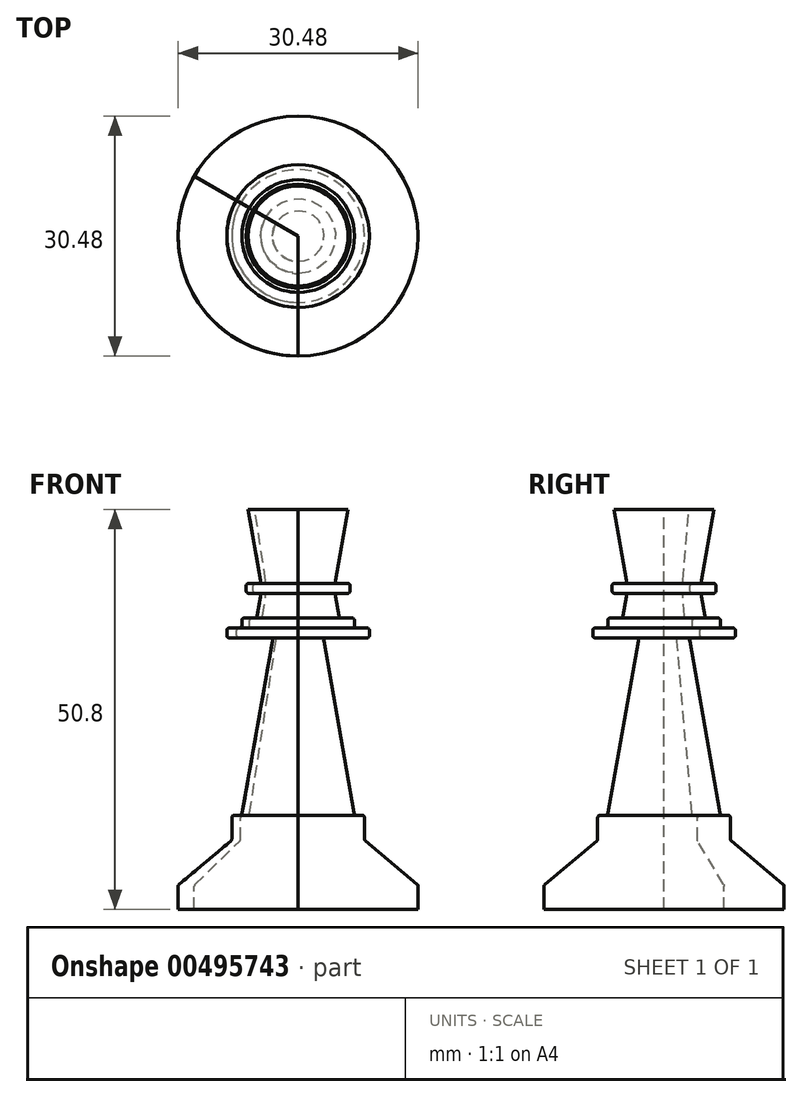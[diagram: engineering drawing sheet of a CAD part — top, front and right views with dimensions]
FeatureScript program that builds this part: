
annotation { "Feature Type Name" : "Feature", "Feature Type Description" : "" }
export const myFeature = defineFeature(function(context is Context, id is Id, definition is map)
    precondition{}
    {
        {
            var Q0;
            Q0=qCreatedBy(makeId("Front.planeOp"),FACE);
            var sketch = newSketch(context, id + "F0", { "sketchPlane" : qUnion([Q0])});
            skLineSegment(sketch, "E0.bottom", {"start": v(0, 0) * mm, "end": v(-15.24, 0) * mm});
            skLineSegment(sketch, "E0.top", {"start": v(0, 50.8) * mm, "end": v(-6.35, 50.8) * mm});
            skLineSegment(sketch, "E0.left", {"start": v(0, 0) * mm, "end": v(0, 50.8) * mm});
            skLineSegment(sketch, "E1", {"start": v(-15.24, 0) * mm, "end": v(-15.24, 2.93) * mm});
            skLineSegment(sketch, "E2", {"start": v(-15.13, 3.18) * mm, "end": v(-8.54, 8.7) * mm});
            skLineSegment(sketch, "E3", {"start": v(-8.43, 8.94) * mm, "end": v(-8.43, 11.65) * mm});
            skLineSegment(sketch, "E4", {"start": v(-8.11, 11.97) * mm, "end": v(-7.43, 11.97) * mm});
            skLineSegment(sketch, "E5", {"start": v(-7.11, 12.23) * mm, "end": v(-3.26, 34.11) * mm});
            skLineSegment(sketch, "E6", {"start": v(-3.57, 34.48) * mm, "end": v(-8.74, 34.48) * mm});
            skLineSegment(sketch, "E7", {"start": v(-9.06, 34.8) * mm, "end": v(-9.06, 35.44) * mm});
            skLineSegment(sketch, "E8", {"start": v(-8.74, 35.75) * mm, "end": v(-7.47, 35.75) * mm});
            skLineSegment(sketch, "E9", {"start": v(-7.15, 36.07) * mm, "end": v(-7.15, 36.7) * mm});
            skLineSegment(sketch, "E10", {"start": v(-6.83, 37.02) * mm, "end": v(-5.51, 37.02) * mm});
            skLineSegment(sketch, "E11", {"start": v(-5.2, 37.29) * mm, "end": v(-4.76, 39.78) * mm});
            skLineSegment(sketch, "E12", {"start": v(-5.07, 40.15) * mm, "end": v(-6.28, 40.15) * mm});
            skLineSegment(sketch, "E13", {"start": v(-6.6, 40.47) * mm, "end": v(-6.6, 41.1) * mm});
            skLineSegment(sketch, "E14", {"start": v(-6.28, 41.42) * mm, "end": v(-5.07, 41.42) * mm});
            skLineSegment(sketch, "E15", {"start": v(-4.76, 41.8) * mm, "end": v(-6.35, 50.8) * mm});
            skPoint(sketch, "E16.visualSharp", {"position": v(-15.24, 3.08) * mm});
            skArc(sketch, "E16.filletArc", {"start": v(-15.13, 3.18) * mm, "mid": v(-15.21, 3.07) * mm, "end": v(-15.24, 2.93) * mm});
            skPoint(sketch, "E17.visualSharp", {"position": v(-8.43, 8.8) * mm});
            skArc(sketch, "E17.filletArc", {"start": v(-8.54, 8.7) * mm, "mid": v(-8.46, 8.8) * mm, "end": v(-8.43, 8.94) * mm});
            skPoint(sketch, "E18.visualSharp", {"position": v(-3.2, 34.48) * mm});
            skArc(sketch, "E18.filletArc", {"start": v(-3.26, 34.11) * mm, "mid": v(-3.33, 34.37) * mm, "end": v(-3.57, 34.48) * mm});
            skPoint(sketch, "E19.visualSharp", {"position": v(-8.43, 11.97) * mm});
            skArc(sketch, "E19.filletArc", {"start": v(-8.11, 11.97) * mm, "mid": v(-8.34, 11.88) * mm, "end": v(-8.43, 11.65) * mm});
            skPoint(sketch, "E20.visualSharp", {"position": v(-7.16, 11.97) * mm});
            skArc(sketch, "E20.filletArc", {"start": v(-7.43, 11.97) * mm, "mid": v(-7.22, 12.04) * mm, "end": v(-7.11, 12.23) * mm});
            skPoint(sketch, "E21.visualSharp", {"position": v(-9.06, 34.48) * mm});
            skArc(sketch, "E21.filletArc", {"start": v(-9.06, 34.8) * mm, "mid": v(-8.96, 34.58) * mm, "end": v(-8.74, 34.48) * mm});
            skPoint(sketch, "E22.visualSharp", {"position": v(-9.06, 35.75) * mm});
            skArc(sketch, "E22.filletArc", {"start": v(-8.74, 35.75) * mm, "mid": v(-8.96, 35.66) * mm, "end": v(-9.06, 35.44) * mm});
            skPoint(sketch, "E23.visualSharp", {"position": v(-7.15, 35.75) * mm});
            skArc(sketch, "E23.filletArc", {"start": v(-7.47, 35.75) * mm, "mid": v(-7.25, 35.85) * mm, "end": v(-7.15, 36.07) * mm});
            skPoint(sketch, "E24.visualSharp", {"position": v(-7.15, 37.02) * mm});
            skArc(sketch, "E24.filletArc", {"start": v(-6.83, 37.02) * mm, "mid": v(-7.06, 36.93) * mm, "end": v(-7.15, 36.7) * mm});
            skPoint(sketch, "E25.visualSharp", {"position": v(-5.25, 37.02) * mm});
            skArc(sketch, "E25.filletArc", {"start": v(-5.51, 37.02) * mm, "mid": v(-5.3, 37.1) * mm, "end": v(-5.2, 37.29) * mm});
            skPoint(sketch, "E26.visualSharp", {"position": v(-4.7, 40.15) * mm});
            skArc(sketch, "E26.filletArc", {"start": v(-4.76, 39.78) * mm, "mid": v(-4.83, 40.04) * mm, "end": v(-5.07, 40.15) * mm});
            skPoint(sketch, "E27.visualSharp", {"position": v(-6.6, 40.15) * mm});
            skArc(sketch, "E27.filletArc", {"start": v(-6.6, 40.47) * mm, "mid": v(-6.5, 40.24) * mm, "end": v(-6.28, 40.15) * mm});
            skPoint(sketch, "E28.visualSharp", {"position": v(-6.6, 41.42) * mm});
            skArc(sketch, "E28.filletArc", {"start": v(-6.28, 41.42) * mm, "mid": v(-6.5, 41.33) * mm, "end": v(-6.6, 41.1) * mm});
            skPoint(sketch, "E29.visualSharp", {"position": v(-4.7, 41.42) * mm});
            skArc(sketch, "E29.filletArc", {"start": v(-5.07, 41.42) * mm, "mid": v(-4.83, 41.53) * mm, "end": v(-4.76, 41.8) * mm});
            skSolve(sketch);
        }
        {
            var Q0;
            Q0=makeQuery(id+"F0.imprint","IMPRINT",FACE,{"disambiguationData":[TD([[makeQuery(id+"F0.imprint","IMPRINT",EDGE,{"derivedFrom":sQuery(id+"F0.wireOp",EDGE,"E0.bottom")}),-1.0]])]});
            var Q1;
            Q1=sQuery(id+"F0.wireOp",EDGE,"E0.left");
            revolve(context, id + "F1", {"entities" : qUnion([Q0]), "axis" : qUnion([Q1]), "revolveType" : RevolveType.TWO_DIRECTIONS, "angle" : 90 * degree, "angleBack" : 330 * degree});
        }
        {
            var Q0;
            Q0=makeQuery(id+"F0.imprint","IMPRINT",FACE,{"disambiguationData":[TD([[makeQuery(id+"F0.imprint","IMPRINT",EDGE,{"derivedFrom":sQuery(id+"F0.wireOp",EDGE,"E0.bottom")}),-1.0]])]});
            var Q1;
            Q1=sQuery(id+"F0.wireOp",EDGE,"E0.left");
            revolve(context, id + "F2", {"entities" : qUnion([Q0]), "axis" : qUnion([Q1]), "revolveType" : RevolveType.FULL});
        }
    });
